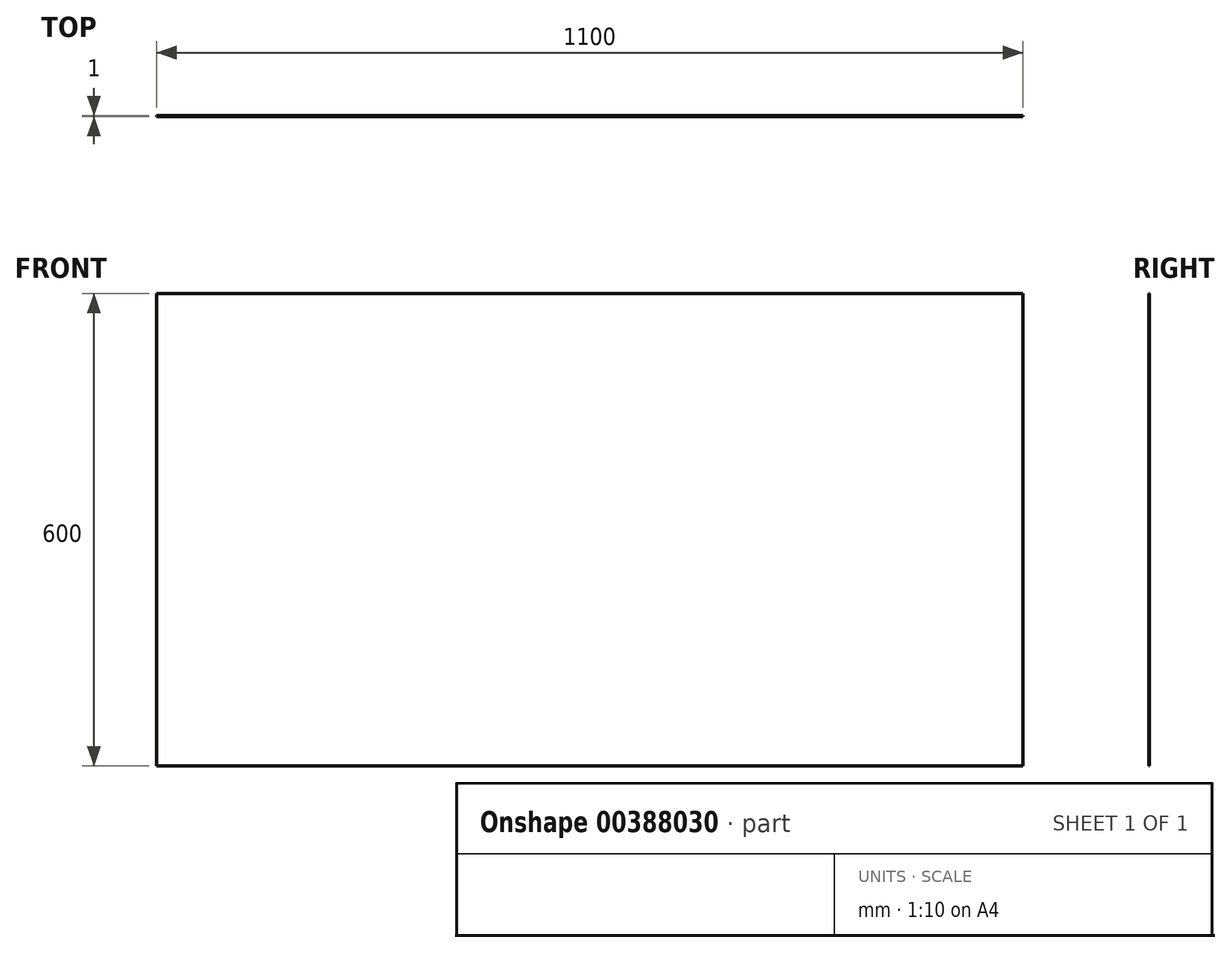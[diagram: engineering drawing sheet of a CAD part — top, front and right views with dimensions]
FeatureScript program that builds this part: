
annotation { "Feature Type Name" : "Feature", "Feature Type Description" : "" }
export const myFeature = defineFeature(function(context is Context, id is Id, definition is map)
    precondition{}
    {
        {
            var Q0;
            Q0=qCreatedBy(makeId("Front.planeOp"),FACE);
            var sketch = newSketch(context, id + "F0", { "sketchPlane" : qUnion([Q0])});
            skLineSegment(sketch, "E0.bottom", {"start": v(0, 0) * mm, "end": v(1100, 0) * mm});
            skLineSegment(sketch, "E0.top", {"start": v(0, 600) * mm, "end": v(1100, 600) * mm});
            skLineSegment(sketch, "E0.left", {"start": v(0, 0) * mm, "end": v(0, 600) * mm});
            skLineSegment(sketch, "E0.right", {"start": v(1100, 0) * mm, "end": v(1100, 600) * mm});
            skSolve(sketch);
        }
        {
            var Q0;
            Q0 = qSketchRegion(id + "F0", true);
            extrude(context, id + "F1", {"entities" : qUnion([Q0]), "depth" : 1 * mm});
        }
    });
